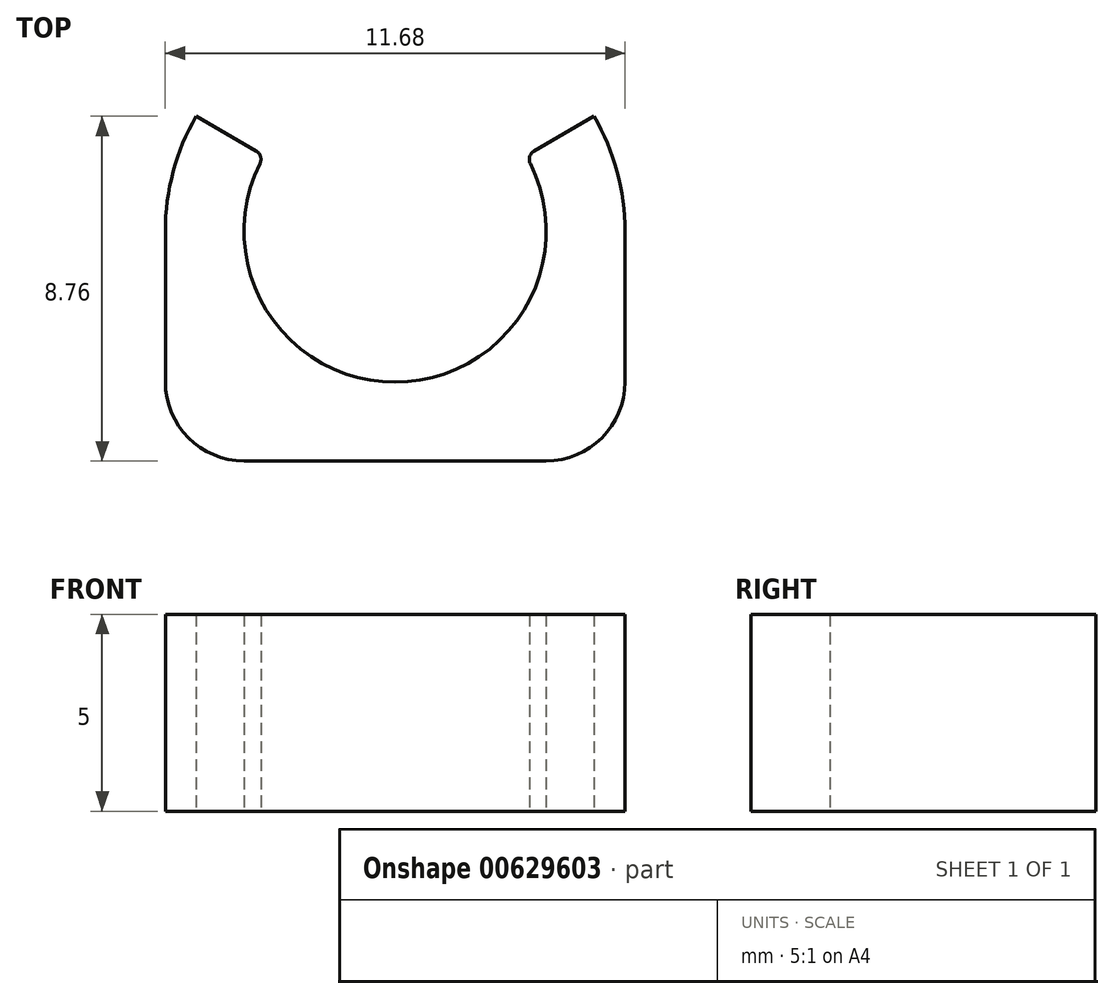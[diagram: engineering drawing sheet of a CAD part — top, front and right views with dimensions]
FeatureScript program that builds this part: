
annotation { "Feature Type Name" : "Feature", "Feature Type Description" : "" }
export const myFeature = defineFeature(function(context is Context, id is Id, definition is map)
    precondition{}
    {
        {
            var Q0;
            Q0=qCreatedBy(makeId("Top.planeOp"),FACE);
            var sketch = newSketch(context, id + "F0", { "sketchPlane" : qUnion([Q0])});
            skArc(sketch, "E0", {"start": v(-3.43, 1.71) * mm, "mid": v(0, -3.84) * mm, "end": v(3.43, 1.71) * mm});
            skArc(sketch, "E1.0", {"start": v(-5.06, 2.92) * mm, "mid": v(0, -5.84) * mm, "end": v(5.06, 2.92) * mm});
            skLineSegment(sketch, "E2", {"start": v(0, -5.84) * mm, "end": v(-3.84, -5.84) * mm});
            skLineSegment(sketch, "E3", {"start": v(0, -5.84) * mm, "end": v(3.84, -5.84) * mm});
            skLineSegment(sketch, "E4", {"start": v(-5.06, 2.92) * mm, "end": v(-3.53, 2.04) * mm});
            skLineSegment(sketch, "E5", {"start": v(3.53, 2.04) * mm, "end": v(5.06, 2.92) * mm});
            skPoint(sketch, "E6.visualSharp", {"position": v(-3.32, 1.92) * mm});
            skArc(sketch, "E6.filletArc", {"start": v(-3.43, 1.71) * mm, "mid": v(-3.42, 1.9) * mm, "end": v(-3.53, 2.04) * mm});
            skPoint(sketch, "E7.visualSharp", {"position": v(3.32, 1.92) * mm});
            skArc(sketch, "E7.filletArc", {"start": v(3.53, 2.04) * mm, "mid": v(3.42, 1.9) * mm, "end": v(3.43, 1.71) * mm});
            skLineSegment(sketch, "E8", {"start": v(-5.84, 0) * mm, "end": v(-5.84, -3.84) * mm});
            skLineSegment(sketch, "E9", {"start": v(5.84, 0) * mm, "end": v(5.84, -3.84) * mm});
            skArc(sketch, "E10.filletArc", {"start": v(-5.84, -3.84) * mm, "mid": v(-5.25, -5.25) * mm, "end": v(-3.84, -5.84) * mm});
            skArc(sketch, "E11.filletArc", {"start": v(3.84, -5.84) * mm, "mid": v(5.25, -5.25) * mm, "end": v(5.84, -3.84) * mm});
            skSolve(sketch);
        }
        {
            var Q0;
            Q0=makeQuery(id+"F0.imprint","IMPRINT",FACE,{"disambiguationData":[TD([[makeQuery(id+"F0.imprint","IMPRINT",EDGE,{"derivedFrom":sQuery(id+"F0.wireOp",EDGE,"E0")}),-1.0]])]});
            var Q1;
            {var subQ0=sQuery(id+"F0.wireOp",EDGE,"E2");Q1=makeQuery(id+"F0.imprint","IMPRINT",FACE,{"disambiguationData":[TD([[makeQuery(id+"F0.imprint","IMPRINT",EDGE,{"derivedFrom":subQ0}),-1.0]])]});}
            var Q2;
            {var subQ0=sQuery(id+"F0.wireOp",EDGE,"E3");Q2=makeQuery(id+"F0.imprint","IMPRINT",FACE,{"disambiguationData":[TD([[makeQuery(id+"F0.imprint","IMPRINT",EDGE,{"derivedFrom":subQ0}),1.0]])]});}
            extrude(context, id + "F1", {"entities" : qUnion([Q0, Q1, Q2]), "depth" : 5 * mm, "offsetDistance" : 25 * mm});
        }
    });
